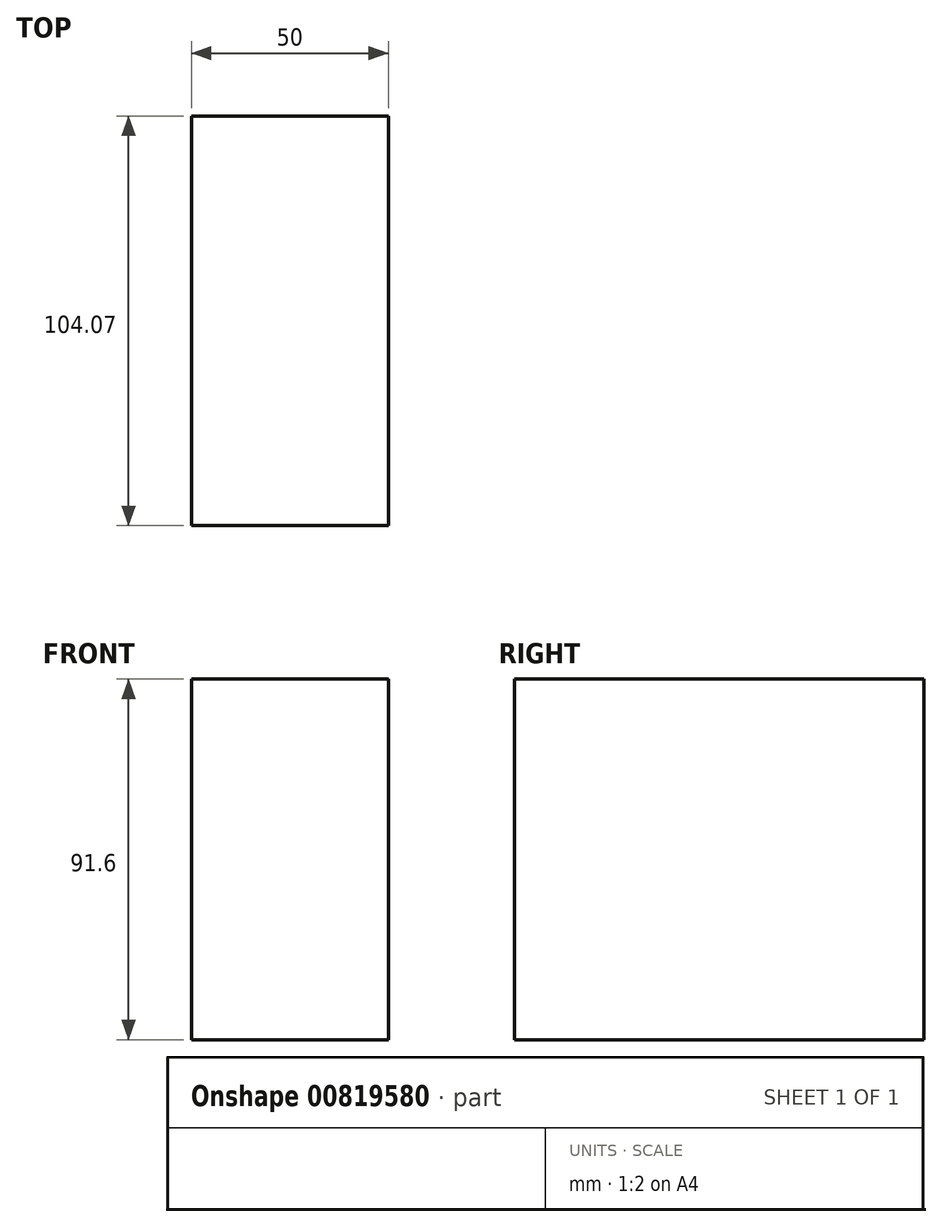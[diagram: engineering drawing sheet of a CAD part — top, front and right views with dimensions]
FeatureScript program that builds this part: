
annotation { "Feature Type Name" : "Feature", "Feature Type Description" : "" }
export const myFeature = defineFeature(function(context is Context, id is Id, definition is map)
    precondition{}
    {
        {
            var Q0;
            Q0=qCreatedBy(makeId("Right.planeOp"),FACE);
            var sketch = newSketch(context, id + "F0", { "sketchPlane" : qUnion([Q0])});
            skLineSegment(sketch, "E0.bottom", {"start": v(-67.68, 39.18) * mm, "end": v(36.39, 39.18) * mm});
            skLineSegment(sketch, "E0.top", {"start": v(-67.68, -52.42) * mm, "end": v(36.39, -52.42) * mm});
            skLineSegment(sketch, "E0.left", {"start": v(-67.68, 39.18) * mm, "end": v(-67.68, -52.42) * mm});
            skLineSegment(sketch, "E0.right", {"start": v(36.39, 39.18) * mm, "end": v(36.39, -52.42) * mm});
            skSolve(sketch);
        }
        {
            var Q0;
            Q0 = qSketchRegion(id + "F0", true);
            extrude(context, id + "F1", {"entities" : qUnion([Q0]), "depth" : 50 * mm, "offsetDistance" : 25 * mm});
        }
    });
